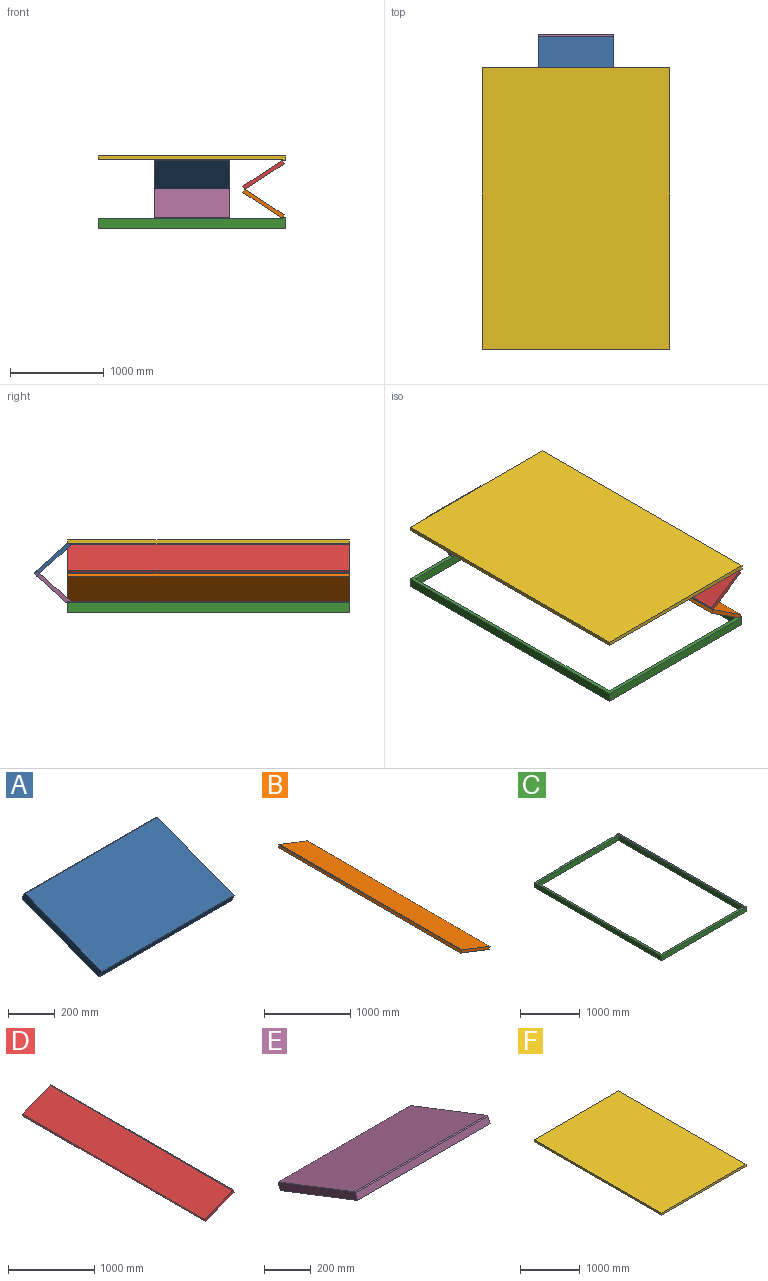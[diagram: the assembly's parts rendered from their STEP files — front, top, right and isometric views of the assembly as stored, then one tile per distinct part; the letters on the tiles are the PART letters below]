
ASSEMBLY  parts=6 mates=9
PART A: 8 faces, bbox 800x480.4x215.1 mm
  f0: cylinder r=5mm len=800mm, axis (-1,0,0), area 6283.2mm2, adj f1,f5,f6,f7
  f1: plane 800x461.27mm, normal (0,-0.36,0.93), area 396000mm2, adj f0,f2,f6,f7
  f2: plane 800x32.62mm, normal (0,-0.93,-0.36), area 28000mm2, adj f1,f3,f6,f7
  f3: cylinder r=5mm len=800mm, axis (-1,0,0), area 6283.2mm2, adj f2,f4,f6,f7
  f4: plane 800x461.27mm, normal (0,0.36,-0.93), area 396000mm2, adj f3,f5,f6,f7
  f5: plane 800x32.62mm, normal (0,0.93,0.36), area 28000mm2, adj f0,f4,f6,f7
  f6: plane 480.44x215.06mm, normal (1,0,0), area 19960.7mm2, adj f0,f1,f2,f3,f4,f5
  f7: plane 480.44x215.06mm, normal (-1,0,0), area 19960.7mm2, adj f0,f1,f2,f3,f4,f5
PART B: 11 faces, bbox 480.4x3000x221.5 mm
  f0: cylinder r=5mm len=3000mm, axis (0,1,0), area 23561.9mm2, adj f1,f8,f9,f10
  f1: plane 3000x32.62mm, normal (0.93,0,-0.36), area 105000mm2, adj f0,f2,f9,f10
  f2: plane 3000x461.27mm, normal (0.36,0,0.93), area 1485000mm2, adj f1,f3,f9,f10
  f3: cylinder r=5mm len=3000mm, axis (0,1,0), area 11138.8mm2, adj f2,f4,f9,f10
  f4: plane 3000x4.66mm, normal (-0.36,0,0.93), area 15000mm2, adj f3,f5,f9,f10
  f5: plane 3000x4.66mm, normal (0.93,0,0.36), area 15000mm2, adj f4,f6,f9,f10
  f6: cylinder r=5mm len=3000mm, axis (0,1,0), area 35985.1mm2, adj f5,f7,f9,f10
  f7: plane 3000x32.62mm, normal (-0.93,0,0.36), area 105000mm2, adj f6,f8,f9,f10
  f8: plane 3000x461.27mm, normal (-0.36,0,-0.93), area 1485000mm2, adj f0,f7,f9,f10
  f9: plane 480.44x221.53mm, normal (0,-1,0), area 20019.6mm2, adj f0,f1,f2,f3,f4,f5,f6,f7
  f10: plane 480.44x221.53mm, normal (0,1,0), area 20019.6mm2, adj f0,f1,f2,f3,f4,f5,f6,f7
PART C: 20 faces, bbox 2000x3000x112.7 mm
  f0: plane 560x40mm, normal (0,0,1), area 22400mm2, adj f6,f9,f11,f18
  f1: plane 3000x35mm, normal (0,0,1), area 105000mm2, adj f2,f7,f8,f9
  f2: cylinder r=5mm len=3000mm, axis (0,1,0), area 17992.6mm2, adj f1,f3,f8,f9
  f3: plane 3000x4.66mm, normal (-0.93,0,0.36), area 15000mm2, adj f2,f4,f8,f9
  f4: plane 3000x4.66mm, normal (0.36,0,0.93), area 15000mm2, adj f3,f5,f8,f9
  f5: cylinder r=5mm len=3000mm, axis (0,1,0), area 29131.3mm2, adj f4,f6,f8,f9
  f6: plane 3000x103mm, normal (-1,0,0), area 301160mm2, adj f0,f5,f8,f9,f10,f11,f14,f15
  f7: plane 3000x108mm, normal (1,0,0), area 324000mm2, adj f1,f8,f9,f15
  f8: plane 2000x112.66mm, normal (0,-1,0), area 196439.3mm2, adj f1,f2,f3,f4,f5,f6,f7,f10
  f9: plane 2000x112.66mm, normal (0,1,0), area 204439.3mm2, adj f0,f1,f2,f3,f4,f5,f6,f7
  f10: plane 3000x1960mm, normal (0,0,1), area 219200mm2, adj f6,f8,f9,f11,f12,f13,f14,f19
  f11: plane 1920x103mm, normal (0,-1,0), area 192160mm2, adj f0,f6,f10,f12,f15,f16,f18,f19
  f12: plane 2920x98mm, normal (1,0,0), area 286160mm2, adj f10,f11,f14,f15
  f13: plane 3000x98mm, normal (-1,0,0), area 294000mm2, adj f8,f9,f10,f15
  f14: plane 1920x98mm, normal (0,1,0), area 188160mm2, adj f6,f10,f12,f15
  f15: plane 3000x2000mm, normal (0,0,-1), area 393600mm2, adj f6,f7,f8,f9,f11,f12,f13,f14
  f16: cylinder r=5mm len=800mm, axis (-1,0,0), area 6283.2mm2, adj f11,f17,f18,f19
  f17: plane 800x35mm, normal (0,0,1), area 28000mm2, adj f9,f16,f18,f19
  f18: plane 40x10mm, normal (1,0,0), area 380.4mm2, adj f0,f9,f11,f16,f17
  f19: plane 40x10mm, normal (-1,0,0), area 380.4mm2, adj f9,f10,f11,f16,f17
PART D: 11 faces, bbox 480.4x3000x221.9 mm
  f0: plane 3000x32.62mm, normal (0.93,0,0.36), area 105000mm2, adj f1,f8,f9,f10
  f1: cylinder r=5mm len=3000mm, axis (0,1,0), area 17992.6mm2, adj f0,f2,f9,f10
  f2: plane 3000x5mm, normal (0,0,1), area 15000mm2, adj f1,f3,f9,f10
  f3: plane 3000x5mm, normal (1,0,0), area 15000mm2, adj f2,f4,f9,f10
  f4: cylinder r=5mm len=3000mm, axis (0,1,0), area 29131.3mm2, adj f3,f5,f9,f10
  f5: plane 3000x461.27mm, normal (-0.36,0,0.93), area 1485000mm2, adj f4,f6,f9,f10
  f6: plane 3000x32.62mm, normal (-0.93,0,-0.36), area 105000mm2, adj f5,f7,f9,f10
  f7: cylinder r=5mm len=3000mm, axis (0,1,0), area 23561.9mm2, adj f6,f8,f9,f10
  f8: plane 3000x461.27mm, normal (0.36,0,-0.93), area 1485000mm2, adj f0,f7,f9,f10
  f9: plane 480.44x221.87mm, normal (0,-1,0), area 20019.6mm2, adj f0,f1,f2,f3,f4,f5,f6,f7
  f10: plane 480.44x221.87mm, normal (0,1,0), area 20019.6mm2, adj f0,f1,f2,f3,f4,f5,f6,f7
PART E: 8 faces, bbox 800x480.4x215.1 mm
  f0: cylinder r=5mm len=800mm, axis (-1,0,0), area 6283.2mm2, adj f1,f5,f6,f7
  f1: plane 800x32.62mm, normal (0,0.93,-0.36), area 28000mm2, adj f0,f2,f6,f7
  f2: plane 800x461.27mm, normal (0,0.36,0.93), area 396000mm2, adj f1,f3,f6,f7
  f3: cylinder r=5mm len=800mm, axis (-1,0,0), area 6283.2mm2, adj f2,f4,f6,f7
  f4: plane 800x32.62mm, normal (0,-0.93,0.36), area 28000mm2, adj f3,f5,f6,f7
  f5: plane 800x461.27mm, normal (0,-0.36,-0.93), area 396000mm2, adj f0,f4,f6,f7
  f6: plane 480.44x215.06mm, normal (1,0,0), area 19960.7mm2, adj f0,f1,f2,f3,f4,f5
  f7: plane 480.44x215.06mm, normal (-1,0,0), area 19960.7mm2, adj f0,f1,f2,f3,f4,f5
PART F: 15 faces, bbox 2000x3000x51.8 mm
  f0: plane 3000x1960mm, normal (0,0,-1), area 5848000mm2, adj f4,f5,f6,f7,f9,f13,f14
  f1: cylinder r=5mm len=3000mm, axis (0,1,0), area 23561.9mm2, adj f2,f4,f5,f6
  f2: plane 3000x35mm, normal (0,0,-1), area 105000mm2, adj f1,f3,f5,f6
  f3: plane 3000x50mm, normal (1,0,0), area 150000mm2, adj f2,f5,f6,f8
  f4: plane 3000x5mm, normal (-1,0,0), area 15000mm2, adj f0,f1,f5,f6
  f5: plane 2000x50mm, normal (0,-1,0), area 80380.4mm2, adj f0,f1,f2,f3,f4,f7,f8
  f6: plane 2000x50mm, normal (0,1,0), area 88380.4mm2, adj f0,f1,f2,f3,f4,f7,f8,f12
  f7: plane 3000x40mm, normal (-1,0,0), area 120000mm2, adj f0,f5,f6,f8
  f8: plane 3000x2000mm, normal (0,0,1), area 6000000mm2, adj f3,f5,f6,f7
  f9: plane 800x5mm, normal (0,-1,0), area 4000mm2, adj f0,f10,f13,f14
  f10: cylinder r=5mm len=800mm, axis (-1,0,0), area 7768.4mm2, adj f9,f11,f13,f14
  f11: plane 800x4.66mm, normal (0,0.36,-0.93), area 4000mm2, adj f10,f12,f13,f14
  f12: plane 800x40mm, normal (0,0,-1), area 32000mm2, adj f6,f11,f13,f14
  f13: plane 45x11.81mm, normal (1,0,0), area 424.3mm2, adj f0,f6,f9,f10,f11,f12
  f14: plane 45x11.81mm, normal (-1,0,0), area 424.3mm2, adj f0,f6,f9,f10,f11,f12
PLACE A rot(axis=(1,0,0),116.6deg) t=(0,2504.46,-498.27)mm
PLACE B rot(axis=(0,1,0),11.7deg) t=(0,0,0)mm
PLACE C at identity fixed
PLACE D rot(axis=(0,-1,0),11.7deg) t=(88.86,0,183.43)mm
PLACE E rot(axis=(-1,0,0),116.6deg) t=(0,2113.33,1305.67)mm
PLACE F t=(0,0,174.31)mm
MATE revolute F.f1 <-> D.f1  axis (0,1,0) through (0,-1500,611.68)mm
MATE parallel F.f8 <-> C.f10  axis (0,0,1) through (-960,0,661.68)mm
MATE planar F.f5 <-> C.f8  axis (0,-1,0) through (-955.36,-1500,641.56)mm
MATE revolute E.f0 <-> C.f16  axis (1,0,0) through (-560,1460,0)mm
MATE revolute A.f0 <-> F.f10  axis (-1,0,0) through (-1360,1460,611.68)mm
MATE revolute B.f0 <-> C.f2  axis (0,-1,0) through (0,-1500,0)mm
MATE revolute D.f7 <-> B.f3  axis (0,1,0) through (-397.57,-1500,305.84)mm
MATE planar F.f3 <-> C.f7  axis (1,0,0) through (40,0,636.68)mm
MATE revolute E.f3 <-> A.f3  axis (-1,0,0) through (-1360,1857.57,305.84)mm
